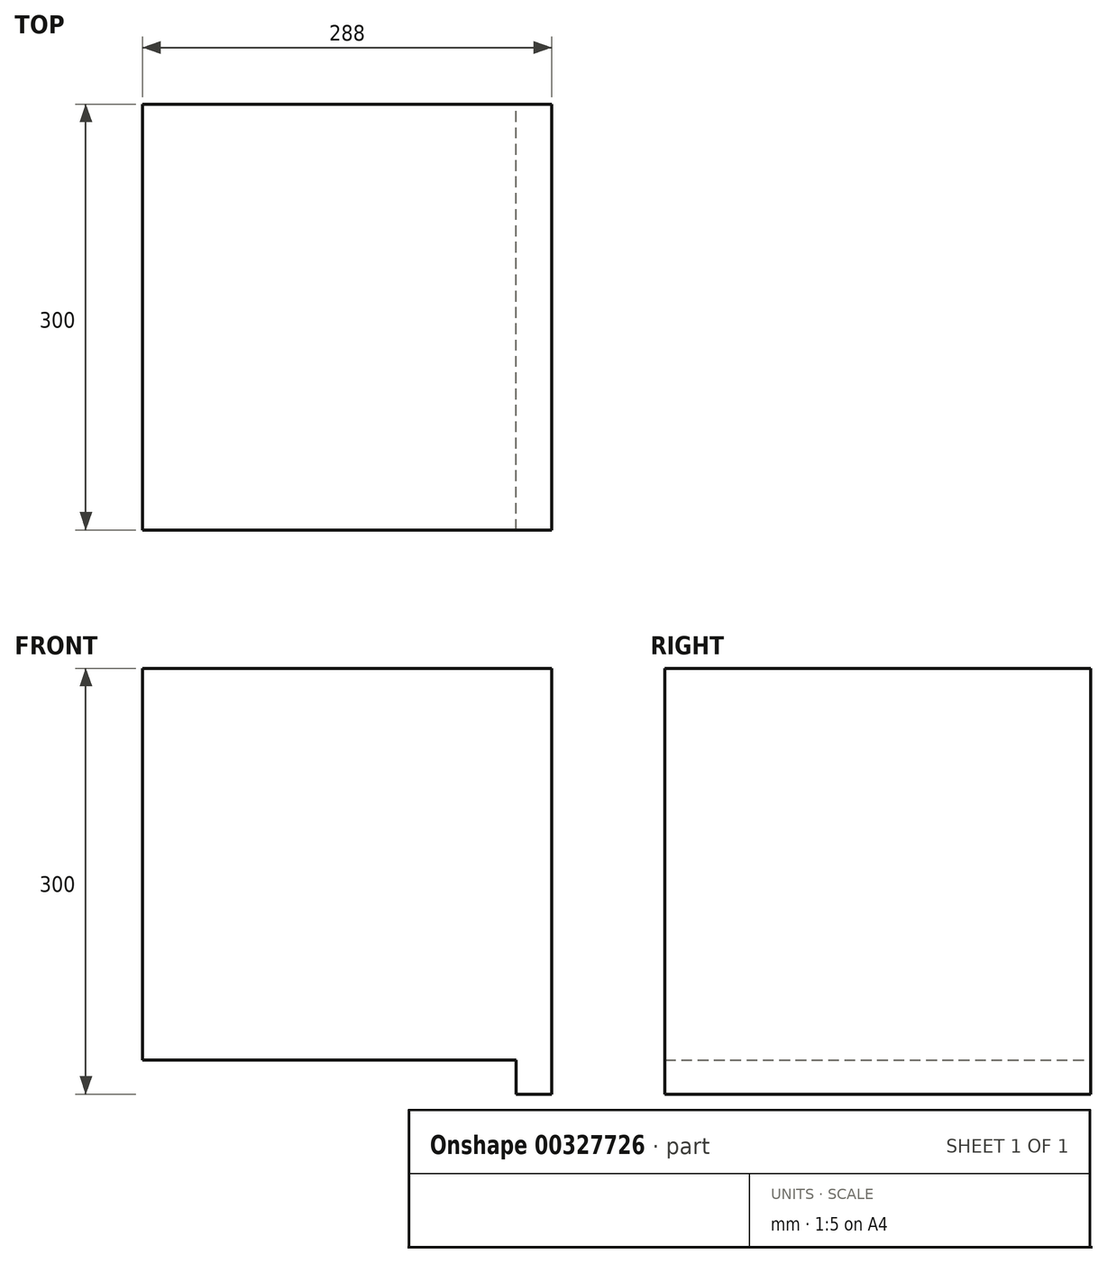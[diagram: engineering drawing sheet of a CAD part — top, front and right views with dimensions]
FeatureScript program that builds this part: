
annotation { "Feature Type Name" : "Feature", "Feature Type Description" : "" }
export const myFeature = defineFeature(function(context is Context, id is Id, definition is map)
    precondition{}
    {
        {
            var Q0;
            Q0=qCreatedBy(makeId("Front.planeOp"),FACE);
            var sketch = newSketch(context, id + "F0", { "sketchPlane" : qUnion([Q0])});
            skLineSegment(sketch, "E0.bottom", {"start": v(-240.7, 239.43) * mm, "end": v(47.3, 239.43) * mm});
            skLineSegment(sketch, "E0.top", {"start": v(22.3, -60.57) * mm, "end": v(47.3, -60.57) * mm});
            skLineSegment(sketch, "E0.left", {"start": v(-240.7, 239.43) * mm, "end": v(-240.7, -36.57) * mm});
            skLineSegment(sketch, "E0.right", {"start": v(47.3, 239.43) * mm, "end": v(47.3, -60.57) * mm});
            skLineSegment(sketch, "E1", {"start": v(22.3, -60.57) * mm, "end": v(22.3, -36.57) * mm});
            skLineSegment(sketch, "E2", {"start": v(22.3, -36.57) * mm, "end": v(-240.7, -36.57) * mm});
            skSolve(sketch);
        }
        {
            var Q0;
            Q0 = qSketchRegion(id + "F0", true);
            extrude(context, id + "F1", {"entities" : qUnion([Q0]), "depth" : 300 * mm});
        }
    });
